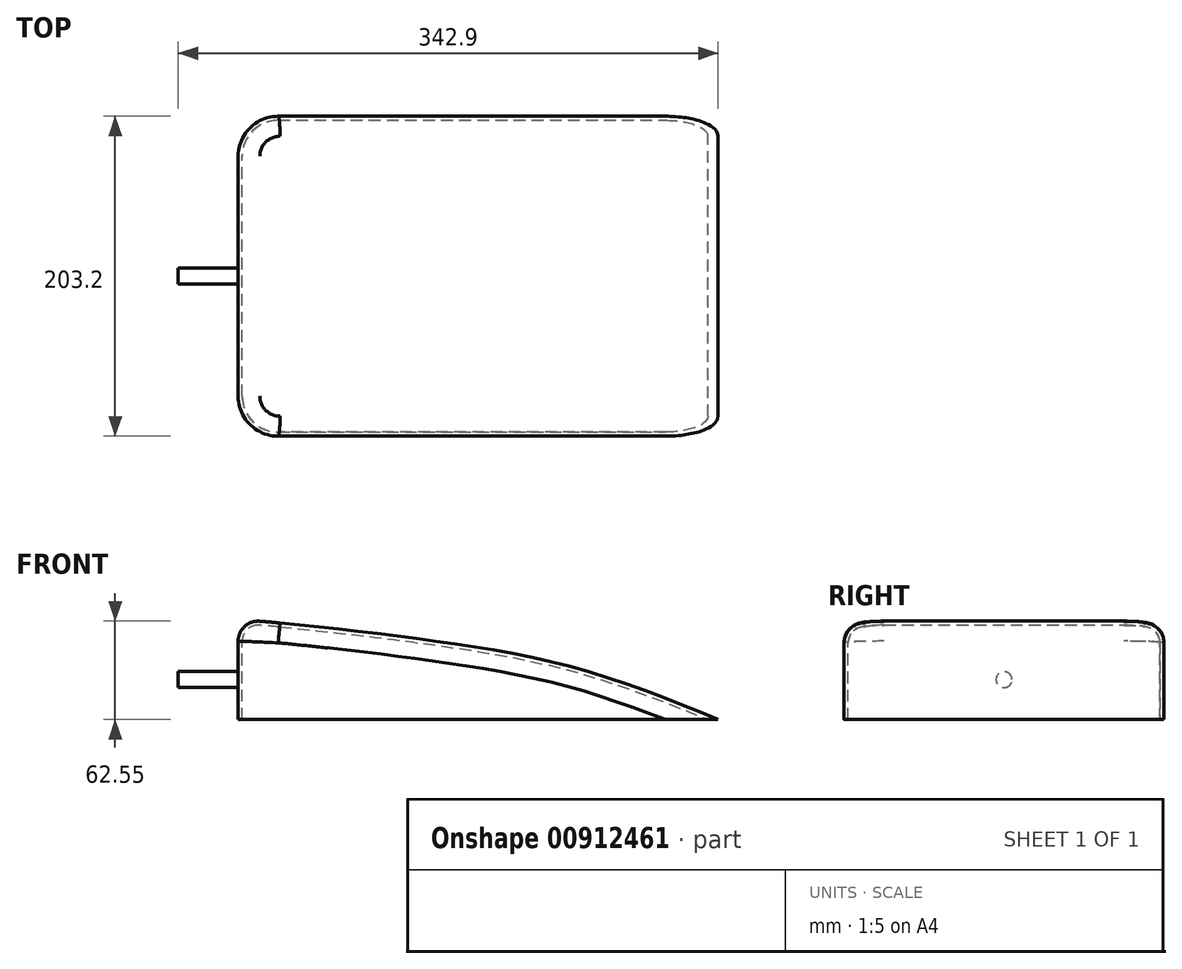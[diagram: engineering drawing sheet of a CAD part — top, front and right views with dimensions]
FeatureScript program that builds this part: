
annotation { "Feature Type Name" : "Feature", "Feature Type Description" : "" }
export const myFeature = defineFeature(function(context is Context, id is Id, definition is map)
    precondition{}
    {
        {
            var Q0;
            Q0=qCreatedBy(makeId("Front.planeOp"),FACE);
            var sketch = newSketch(context, id + "F0", { "sketchPlane" : qUnion([Q0])});
            skLineSegment(sketch, "E0", {"start": v(-148.68, -41.84) * mm, "end": v(156.12, -41.84) * mm});
            skLineSegment(sketch, "E1", {"start": v(-148.68, -41.84) * mm, "end": v(-148.68, 21.66) * mm});
            skFitSpline(sketch, "E2", {"points": [v(-148.68, 21.66) * mm, v(-91.72, 16.47) * mm, v(-7.26, 5.7) * mm, v(69.81, -10.19) * mm, v(156.12, -41.84) * mm], "startDerivative": vector(254.4, -16.43) * mm, "endDerivative": vector(317.72, -134.5) * mm});
            skSolve(sketch);
        }
        {
            var Q0;
            Q0 = qSketchRegion(id + "F0", true);
            extrude(context, id + "F1", {"entities" : qUnion([Q0]), "depth" : 203.2 * mm, "offsetDistance" : 25.4 * mm});
        }
        {
            var Q0;
            Q0=makeQuery(id+"F1.opExtrude","SWEPT_EDGE",EDGE,{"disambiguationData":[OSD([sQuery(id+"F0.wireOp",EDGE,"E1"),sQuery(id+"F0.wireOp",EDGE,"E2")])]});
            var Q1;
            Q1=makeQuery(id+"F1.opExtrude","CAP_EDGE",EDGE,{"disambiguationData":[OSD([sQuery(id+"F0.wireOp",EDGE,"E2")])],"isStart":false});
            var Q2;
            Q2=makeQuery(id+"F1.opExtrude","CAP_EDGE",EDGE,{"disambiguationData":[OSD([sQuery(id+"F0.wireOp",EDGE,"E2")])],"isStart":true});
            fillet(context, id + "F2", {"entities" : qUnion([Q0, Q1, Q2]), "radius" : 12.7 * mm, "tangentPropagation" : true, "allowEdgeOverflow" : false});
        }
        {
            var Q0;
            Q0=makeQuery(id+"F1.opExtrude","CAP_EDGE",EDGE,{"disambiguationData":[OSD([sQuery(id+"F0.wireOp",EDGE,"E1")])],"isStart":false});
            var Q1;
            Q1=makeQuery(id+"F1.opExtrude","CAP_EDGE",EDGE,{"disambiguationData":[OSD([sQuery(id+"F0.wireOp",EDGE,"E1")])],"isStart":true});
            fillet(context, id + "F3", {"entities" : qUnion([Q0, Q1]), "radius" : 25.4 * mm, "tangentPropagation" : true, "allowEdgeOverflow" : false});
        }
        {
            var Q0;
            Q0=makeQuery(id+"F1.opExtrude","SWEPT_FACE",FACE,{"disambiguationData":[OSD([sQuery(id+"F0.wireOp",EDGE,"E0")])]});
            shell(context, id + "F4", {"entities" : qUnion([Q0]), "thickness" : 2.54 * mm});
        }
        {
            var Q0;
            Q0=makeQuery(id+"F1.opExtrude","SWEPT_FACE",FACE,{"disambiguationData":[OSD([sQuery(id+"F0.wireOp",EDGE,"E1")])]});
            var sketch = newSketch(context, id + "F5", { "sketchPlane" : qUnion([Q0])});
            skCircle(sketch, "E3", {"center": v(101.6, -16.44) * mm, "radius": 5.08 * mm});
            skSolve(sketch);
        }
        {
            var Q0;
            Q0 = qSketchRegion(id + "F5", true);
            extrude(context, id + "F6", {"entities" : qUnion([Q0]), "operationType" : NewBodyOperationType.ADD, "depth" : 38.1 * mm, "offsetDistance" : 25.4 * mm});
        }
    });
